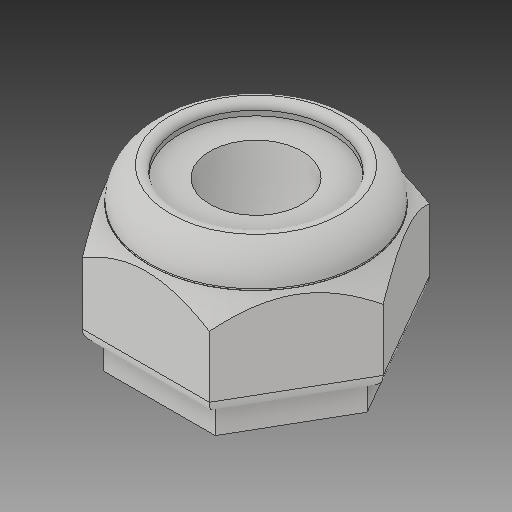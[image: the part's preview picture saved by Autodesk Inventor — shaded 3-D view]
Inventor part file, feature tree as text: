
AUTODESK INVENTOR PART (.ipt)
format: ipt  version: 2017 (Build 210142000, 142)  size: 167,424 bytes
history: native  units: in
note: dims shown in document units (in); Inventor stores cm internally (conversion verified against a paired STEP export)
features: extrude x1
ambient origin geometry x8: Origin, YZ Plane, XZ Plane, XY Plane, X Axis, Y Axis, Z Axis, Center Point
bodies: Solid1 (feature_tree)
feature tree (1):
  extrude  "Extrude1"  [1 undecoded]
note: 1 required parameter value undecoded (feature->parameter linkage not recoverable at this tier; creation-order binding heuristic only, values carry confidence <= 0.55)
